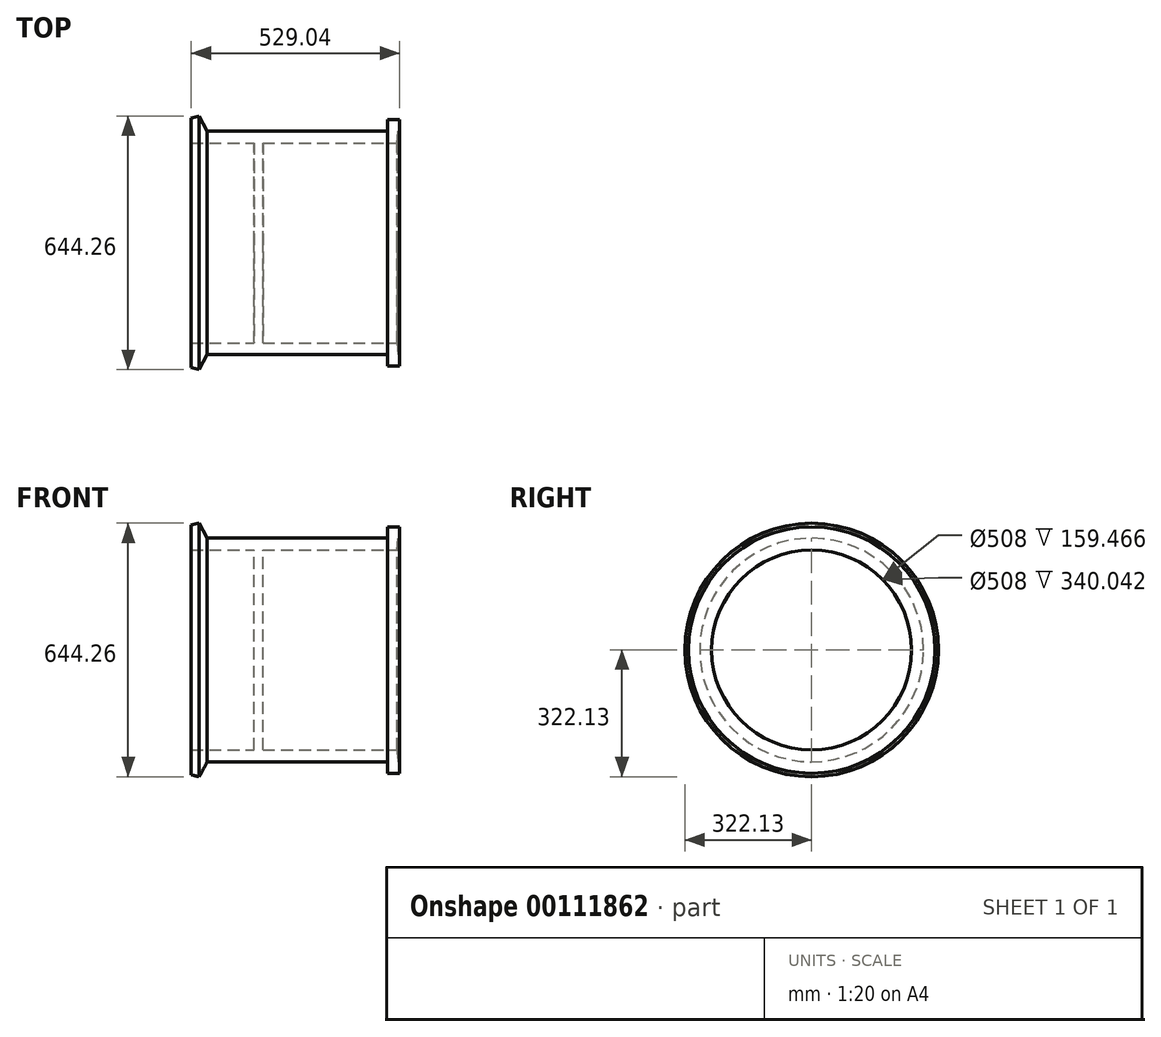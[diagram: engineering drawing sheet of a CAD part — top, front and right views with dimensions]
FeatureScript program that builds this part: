
annotation { "Feature Type Name" : "Feature", "Feature Type Description" : "" }
export const myFeature = defineFeature(function(context is Context, id is Id, definition is map)
    precondition{}
    {
        {
            var Q0;
            Q0=qCreatedBy(makeId("Front.planeOp"),FACE);
            var sketch = newSketch(context, id + "F0", { "sketchPlane" : qUnion([Q0])});
            skLineSegment(sketch, "E0", {"start": v(-220.93, 317.12) * mm, "end": v(-220.93, 254) * mm});
            skLineSegment(sketch, "E1", {"start": v(-220.93, 254) * mm, "end": v(-61.47, 254) * mm});
            skLineSegment(sketch, "E2", {"start": v(301.1, 254) * mm, "end": v(308.1, 313.12) * mm});
            skLineSegment(sketch, "E3", {"start": v(308.1, 313.12) * mm, "end": v(278.05, 313.12) * mm});
            skLineSegment(sketch, "E4", {"start": v(278.05, 313.12) * mm, "end": v(278.05, 284.06) * mm});
            skLineSegment(sketch, "E5", {"start": v(278.05, 284.06) * mm, "end": v(-180.86, 284.06) * mm});
            skLineSegment(sketch, "E6", {"start": v(-180.86, 284.06) * mm, "end": v(-200.9, 322.13) * mm});
            skLineSegment(sketch, "E7", {"start": v(-200.9, 322.13) * mm, "end": v(-220.93, 317.12) * mm});
            skLineSegment(sketch, "E8", {"start": v(0, 0) * mm, "end": v(-221.94, 0) * mm, "construction": true});
            skLineSegment(sketch, "E9", {"start": v(-61.47, 254) * mm, "end": v(-61.47, 0) * mm});
            skLineSegment(sketch, "E10", {"start": v(-61.47, 0) * mm, "end": v(-38.95, 0) * mm});
            skLineSegment(sketch, "E11", {"start": v(-38.95, 0) * mm, "end": v(-38.95, 254) * mm});
            skLineSegment(sketch, "E12.trimOffspring", {"start": v(-38.95, 254) * mm, "end": v(301.1, 254) * mm});
            skSolve(sketch);
        }
        {
            var Q0;
            Q0=makeQuery(id+"F0.imprint","IMPRINT",FACE,{"disambiguationData":[TD([[makeQuery(id+"F0.imprint","IMPRINT",EDGE,{"derivedFrom":sQuery(id+"F0.wireOp",EDGE,"E0")}),1.0]])]});
            var Q1;
            Q1=sQuery(id+"F0.wireOp",EDGE,"E8");
            revolve(context, id + "F1", {"entities" : qUnion([Q0]), "axis" : qUnion([Q1]), "revolveType" : RevolveType.FULL});
        }
    });
